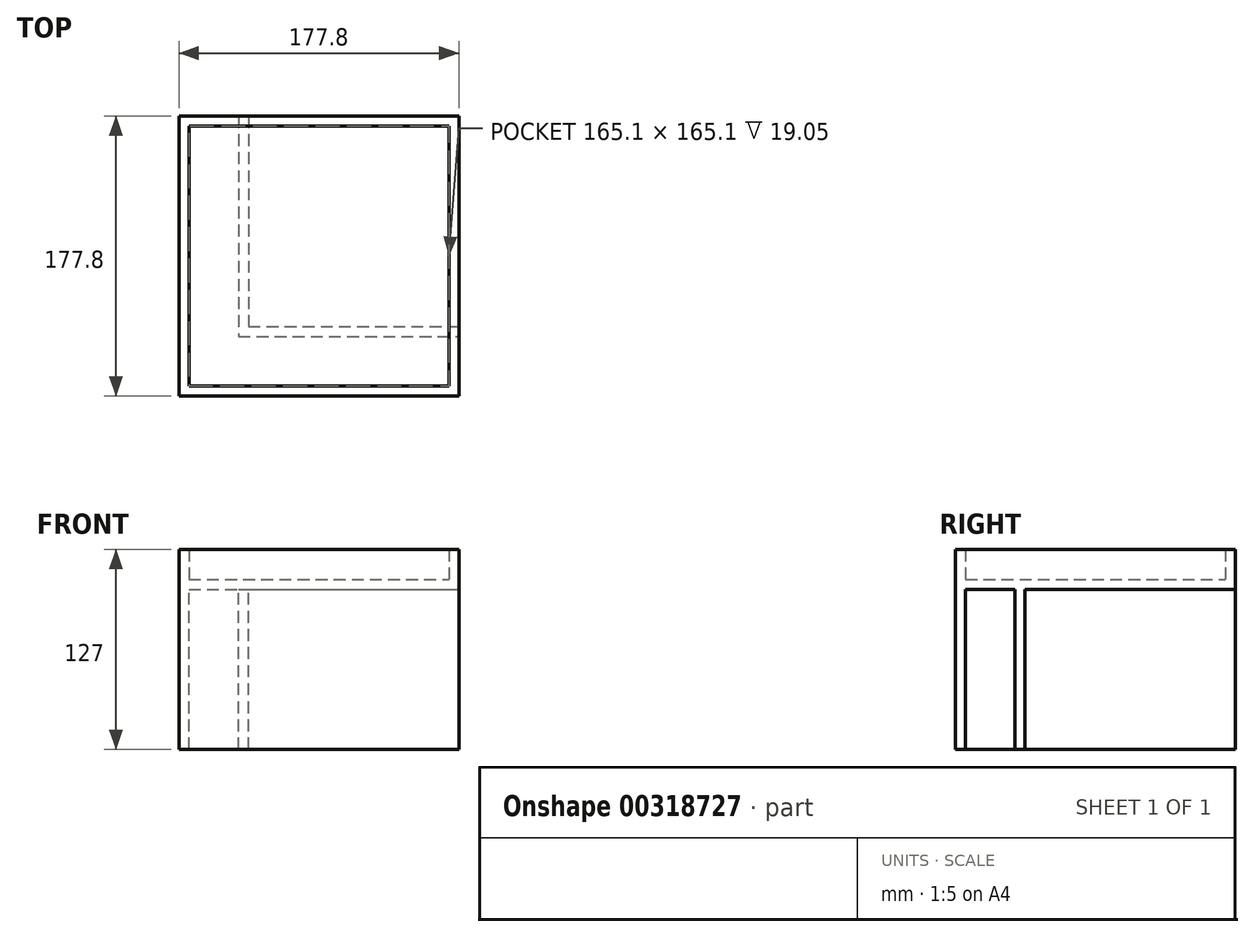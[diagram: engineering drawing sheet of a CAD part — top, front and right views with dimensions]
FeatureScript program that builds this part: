
annotation { "Feature Type Name" : "Feature", "Feature Type Description" : "" }
export const myFeature = defineFeature(function(context is Context, id is Id, definition is map)
    precondition{}
    {
        {
            var Q0;
            Q0=qCreatedBy(makeId("Top.planeOp"),FACE);
            var sketch = newSketch(context, id + "F0", { "sketchPlane" : qUnion([Q0])});
            skLineSegment(sketch, "E0.bottom", {"start": v(0, 0) * mm, "end": v(177.8, 0) * mm});
            skLineSegment(sketch, "E0.top", {"start": v(0, 177.8) * mm, "end": v(177.8, 177.8) * mm});
            skLineSegment(sketch, "E0.left", {"start": v(0, 0) * mm, "end": v(0, 177.8) * mm});
            skLineSegment(sketch, "E0.right", {"start": v(177.8, 0) * mm, "end": v(177.8, 177.8) * mm});
            skLineSegment(sketch, "E1.bottom", {"start": v(6.35, 6.35) * mm, "end": v(171.45, 6.35) * mm});
            skLineSegment(sketch, "E1.top", {"start": v(6.35, 171.45) * mm, "end": v(171.45, 171.45) * mm});
            skLineSegment(sketch, "E1.left", {"start": v(6.35, 6.35) * mm, "end": v(6.35, 171.45) * mm});
            skLineSegment(sketch, "E1.right", {"start": v(171.45, 6.35) * mm, "end": v(171.45, 171.45) * mm});
            skSolve(sketch);
        }
        {
            var Q0;
            Q0 = qSketchRegion(id + "F0", true);
            extrude(context, id + "F1", {"entities" : qUnion([Q0]), "depth" : 25.4 * mm, "offsetDistance" : 25.4 * mm});
        }
        {
            var Q0;
            Q0=makeQuery(id+"F0.imprint","IMPRINT",FACE,{"disambiguationData":[TD([[makeQuery(id+"F0.imprint","IMPRINT",EDGE,{"derivedFrom":sQuery(id+"F0.wireOp",EDGE,"E1.bottom")}),1.0]])]});
            extrude(context, id + "F2", {"entities" : qUnion([Q0]), "operationType" : NewBodyOperationType.ADD, "depth" : 6.35 * mm, "offsetDistance" : 25.4 * mm});
        }
        {
            var Q0;
            {var subQ0=sQuery(id+"F0.wireOp",EDGE,"E1.right");var subQ1=sQuery(id+"F0.wireOp",EDGE,"E1.left");var subQ2=sQuery(id+"F0.wireOp",EDGE,"E1.top");var subQ3=sQuery(id+"F0.wireOp",EDGE,"E1.bottom");Q0=makeQuery(id+"F2.boolean.opBoolean","MERGE",FACE,{"derivedFrom":[makeQuery(id+"F1.opExtrude","CAP_FACE",FACE,{"disambiguationData":[OSD([sQuery(id+"F0.wireOp",EDGE,"E0.bottom"),sQuery(id+"F0.wireOp",EDGE,"E0.top"),sQuery(id+"F0.wireOp",EDGE,"E0.left"),sQuery(id+"F0.wireOp",EDGE,"E0.right"),subQ3,subQ2,subQ1,subQ0])],"isStart":true}),makeQuery(id+"F2.opExtrude","CAP_FACE",FACE,{"disambiguationData":[OSD([subQ3,subQ2,subQ1,subQ0])],"isStart":true})]});}
            var sketch = newSketch(context, id + "F3", { "sketchPlane" : qUnion([Q0])});
            skLineSegment(sketch, "E2", {"start": v(0, 0) * mm, "end": v(177.8, 0) * mm});
            skLineSegment(sketch, "E3", {"start": v(177.8, 0) * mm, "end": v(177.8, -6.35) * mm});
            skLineSegment(sketch, "E4", {"start": v(0, 0) * mm, "end": v(0, -177.8) * mm});
            skLineSegment(sketch, "E5", {"start": v(0, -177.8) * mm, "end": v(6.35, -177.8) * mm});
            skLineSegment(sketch, "E6", {"start": v(6.35, -177.8) * mm, "end": v(6.35, -6.35) * mm});
            skLineSegment(sketch, "E7", {"start": v(6.35, -6.35) * mm, "end": v(177.8, -6.35) * mm});
            skSolve(sketch);
        }
        {
            var Q0;
            Q0 = qSketchRegion(id + "F3", true);
            extrude(context, id + "F4", {"entities" : qUnion([Q0]), "operationType" : NewBodyOperationType.ADD, "depth" : 101.6 * mm, "offsetDistance" : 25.4 * mm});
        }
        {
            var Q0;
            {var subQ0=sQuery(id+"F0.wireOp",EDGE,"E1.right");var subQ1=sQuery(id+"F0.wireOp",EDGE,"E1.left");var subQ2=sQuery(id+"F0.wireOp",EDGE,"E1.top");var subQ3=sQuery(id+"F0.wireOp",EDGE,"E1.bottom");Q0=makeQuery(id+"F2.boolean.opBoolean","MERGE",FACE,{"derivedFrom":[makeQuery(id+"F1.opExtrude","CAP_FACE",FACE,{"disambiguationData":[OSD([sQuery(id+"F0.wireOp",EDGE,"E0.bottom"),sQuery(id+"F0.wireOp",EDGE,"E0.top"),sQuery(id+"F0.wireOp",EDGE,"E0.left"),sQuery(id+"F0.wireOp",EDGE,"E0.right"),subQ3,subQ2,subQ1,subQ0])],"isStart":true}),makeQuery(id+"F2.opExtrude","CAP_FACE",FACE,{"disambiguationData":[OSD([subQ3,subQ2,subQ1,subQ0])],"isStart":true})]});}
            var sketch = newSketch(context, id + "F5", { "sketchPlane" : qUnion([Q0])});
            skLineSegment(sketch, "E8", {"start": v(37.85, -177.8) * mm, "end": v(37.85, -37.85) * mm});
            skLineSegment(sketch, "E9", {"start": v(37.85, -37.85) * mm, "end": v(177.8, -37.85) * mm});
            skLineSegment(sketch, "E10", {"start": v(44.2, -177.8) * mm, "end": v(44.2, -44.2) * mm});
            skLineSegment(sketch, "E11", {"start": v(44.2, -44.2) * mm, "end": v(177.8, -44.2) * mm});
            skLineSegment(sketch, "E12", {"start": v(37.85, -177.8) * mm, "end": v(44.2, -177.8) * mm});
            skLineSegment(sketch, "E13", {"start": v(177.8, -44.2) * mm, "end": v(177.8, -37.85) * mm});
            skSolve(sketch);
        }
        {
            var Q0;
            Q0 = qSketchRegion(id + "F5", true);
            extrude(context, id + "F6", {"entities" : qUnion([Q0]), "operationType" : NewBodyOperationType.ADD, "depth" : 101.6 * mm, "offsetDistance" : 25.4 * mm});
        }
    });
